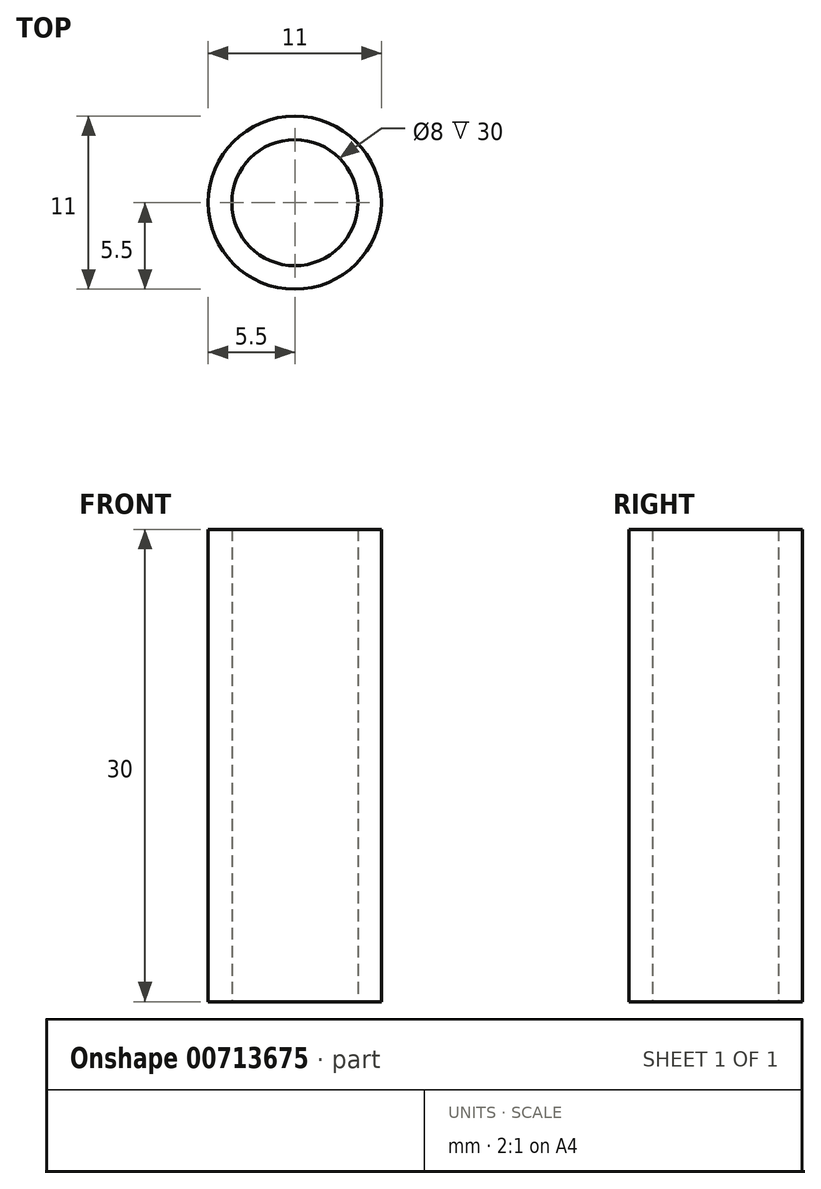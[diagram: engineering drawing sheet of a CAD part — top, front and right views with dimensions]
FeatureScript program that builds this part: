
annotation { "Feature Type Name" : "Feature", "Feature Type Description" : "" }
export const myFeature = defineFeature(function(context is Context, id is Id, definition is map)
    precondition{}
    {
        {
            var Q0;
            Q0=qCreatedBy(makeId("Top.planeOp"),FACE);
            var sketch = newSketch(context, id + "F0", { "sketchPlane" : qUnion([Q0])});
            skCircle(sketch, "E0", {"center": v(0, 0) * mm, "radius": 5.5 * mm});
            skCircle(sketch, "E1", {"center": v(0, 0) * mm, "radius": 4 * mm});
            skSolve(sketch);
        }
        {
            var Q0;
            Q0=makeQuery(id+"F0.imprint","IMPRINT",FACE,{"disambiguationData":[TD([[makeQuery(id+"F0.imprint","IMPRINT",EDGE,{"derivedFrom":sQuery(id+"F0.wireOp",EDGE,"E0")}),1.0]])]});
            extrude(context, id + "F1", {"entities" : qUnion([Q0]), "depth" : 30 * mm, "offsetDistance" : 25 * mm});
        }
    });
